# Revit family: Gira_210427
name_source: partatom
category: Elektroinstallationen
revit_build: Autodesk Revit 2017 (Build: 20160225_1515(x64)
units: mm (PartAtom-declared; Revit-internal decimal feet)

## family parameters
Basisbauteil = Fläche
Beim Laden mit Abzugskörper schneiden = Nein
Bemaßung runder Anschluss = Durchmesser verwenden
Beschriftungsausrichtung beibehalten = Nein
Gemeinsam genutzt = Nein
Raumberechnungspunkt = Nein
Teiletyp = Normal

## types (1)
- Gira_210427
    Acoustic signal = Ja
    Analogue input = Nein
    BIM = https://media.stage.bim.site und Tasten.rfa
    Beschreibung = KNX CO2 sens.humidity RTC Sys55 PWm,KNX CO2 sensor with humidity and room temperature controller,System 55,pure white matt,CO?-sensor with an integrated KNX bus coupler and two binary inputs for measuring the concentration of carbon dioxide, relative humidity, and room temperature.,,Features:,- Limit value monitoring for CO2 concentration and humidity,- Dewpoint alert e.g. for cooling ceilings and winter gardens to prevent possible mould growth.,- Two binary inputs for connecting zero-voltage contacts.,- Logic gates for easy linking functions.,Sensor:,- Up to four different limits can be set for the CO2-sensor.,- Adaptation to current sea level above NN.,- Up to two limits can be set for the humidity sensor.,Controller:,- 5 operating modes: Komfort, standby, night, frost or heat protection, and controller lock-out (e.g. dew-point mode).,- Heating cooling functions: Heating, cooling, heating and cooling, basic and additional heating, basic and additional cooling.,- Preset control parameters for common radiators or cooling units.,- Controller deactivatable (dewpoint operation) or controller or operation of the controller can be blocked.,- Valve protection function (valve is opened cyclically every 24 hours).,- Control types: continuous PI control, switching PI control (PWM), and switching 2-point control (on off).,Inputs:,- Free assignment of the functions switching, dimming, blind and value transmitter to the inputs.,- Blocker for blocking individual inputs.,- Behaviour can be configured following bus voltage recovery.,- Telegram rate limit.,- Switching function: two independent switching objects are available for each existing input and can be enabled individually, command for leading and trailing edge can be set independently (ON, OFF, CHANGE, no reaction).,- Dimming function: single-surface and double-surface operation, time between dimming and switching, and dim-step size can be set, telegram repetition and stop telegram transmission possible.,- Blind function: command can be set with rising edge (no function, UP, DOWN, SW), operating concept can be parameterised, time between short and long-term operation adjustable, slat adjustment time adjustable.,- Value transmitter and light scene auxiliary unit function: edge (button as NO contact, button as NC contact, switch) and value with edge can be configured, value adjustment by pressing and holding a button for value transmitters possible, light scene auxiliary unit with without memory function.,,Notes :,- The CO2-sensor does not have any operating or display elements.,- The use of a switch terminal box for connection of the external inputs is recommended.,- A separate bus coupler is not required to operate the CO2-sensor.
    Bus connection included = Nein
    Bus system KNX = Ja
    Bus system KNX radio = Nein
    Bus system LON = Nein
    Bus system Powernet = Nein
    Bus system radio frequent = Nein
    Colour = White
    Data sheet = https://katalog.gira.de
    Degree of protection (IP) = IP20
    GTIN = 4010337084495
    HAN = 210427
    Hersteller = Gira
    Material = Other
    Material quality = Other
    Model = CO2-Sensor
    Mounting method = Flush mounted (plaster)
    Number of channels = 3
    Other bus systems = None
    Productwebsite = http://katalog.gira.de
    RAL-number (akin) = 9010
    Surface finishing = Glossy
    Surface protection = Other
    Transparent = Nein
    Typname = KNX CO? sensor humidity cont. + RTC System 55 p.white m
    URL = https://www.gira.de
    Vorgabe-Ansicht = 1219 mm
    Weather station = Nein
    With DCF77 = Nein
    With heating = Nein

## geometry (parser evidence)
native form markers: Sweep x7
no freeform markers — native parametric forms only
